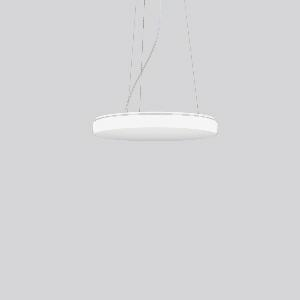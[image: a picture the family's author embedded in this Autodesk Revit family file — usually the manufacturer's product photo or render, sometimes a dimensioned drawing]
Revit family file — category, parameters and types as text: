
# Revit family: flat_polymero_kreis_slim_312091_002_4_d000
name_source: partatom
category: Lighting Fixtures
units: mm (PartAtom-declared; Revit-internal decimal feet)

## family parameters
Cut with Voids When Loaded = No
Host = Face
Light Source = No
Part Type = Normal
Room Calculation Point = No
Round Connector Dimension = Use Diameter
Shared = No

## types (1)
- FLAT POLYMERO KREIS SLIM (1 x LED Modul 840, 3500 lm, 4000)
    Apparent Load = 28 VA
    CIE Flux Codes = 42 73 92 86 100
    Color Rendering = 80
    Color Temperature = 4000
    Default Elevation = 1800 mm
    Description = Series: FLAT POLYMERO KREIS SLIM
Decorative round LED pendant luminaire. Base and canopy: metal, powder-coated, white. Canopy Ø 205 mm, h 35 mm. Diffuser made of plastic (polycarbonate), opal, shockproof. Diffuser fastening: patented push system. Homogeneous and smooth light distribution. Suitable for pendant. 3-point steel cable suspension, steplessly adjustable. Special lengths available on request. 
Colour: white
Diameter: 515 mm
Height: 69 mm
Suspension length: 350-1300 mm
Lamp: LED
Socket: without socket
Colour temperature: 4000K
Colour rendering index (CRI): 83
System power: 28 W
Rated luminous flux: 3500 lm
Luminous efficiency: 125 lm/W
Control gear: AC Strom, dim.Ph.an-/abschnitt
Protection class: I
Type of protection: IP 40
    Height = 69 mm
    Lamp = 1 x LED Modul 840
    Lamp Light Flux = 3500 lm
    Lamp count = 1
    Length = 515 mm
    Lifetime = 50000 h
    Luminous efficacy = 125 lm/W
    Manufacturer = RZB
    ModVariant = No
    Model = 312091.002.4
    Mounting Place = Ceiling
    Mounting Type = Pendant
    Number of Poles = 1
    OnlyDefault = Yes
    Power Factor = 1
    Product Name = FLAT POLYMERO KREIS SLIM
    Product group = Pendant luminaires
    ProductGroupID = 902
    Protection Class = Protection class I
    Protection Degree = IP 40
    RLX_Detail_Level = 1
    RLX_Emergency_Light_Flux = 0 lm
    RLX_Emergency_Type = 0
    RLX_Emergency_Type_DB = No
    RlxData = <blob elided: 42525 chars, md5=82fa6597>
    Socket = socket
    Standby Power = 0 W
    System Light Flux = 3500 lm
    System Power = 28 W
    Type Comments = Product without accessories
    Type Image = 312091.002.jpg
    URL = http://relux.com
    VarID = ---
    Voltage = 230 V
    Voltage Range = 220-240 V
    Weight = 0.00 kg
    Width = 0 mm  [stored 0 ft]

note: [stored X ft] marks values corroborated as IEEE doubles in the binary element streams (Revit-internal decimal feet)

## geometry (parser evidence)
native form markers: Blend x4, Sweep x10
no freeform markers — native parametric forms only
